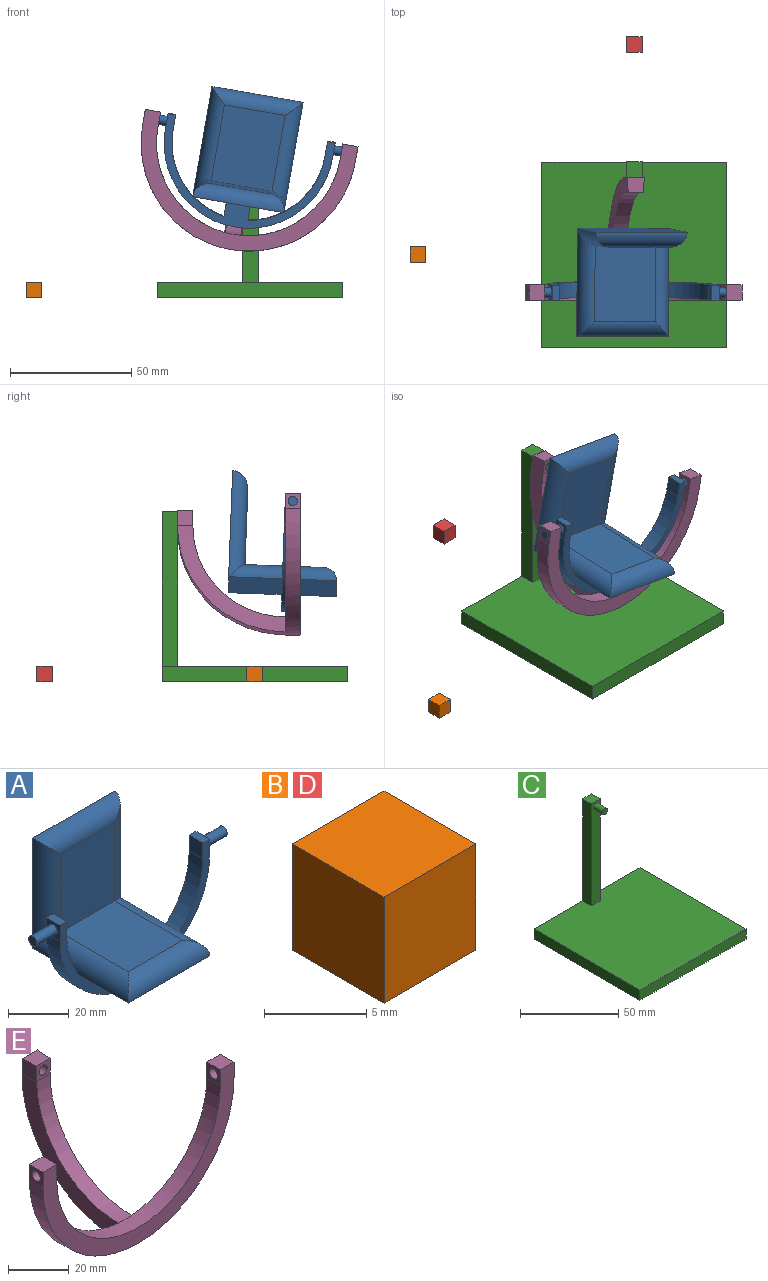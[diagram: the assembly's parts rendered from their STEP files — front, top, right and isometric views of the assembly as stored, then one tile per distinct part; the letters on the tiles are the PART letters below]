
ASSEMBLY  parts=5 mates=4
PART A: 27 faces, bbox 88.9x44.5x54.4 mm
  f0: plane 31.75x25.4mm, normal (0,0,1), area 806.5mm2, adj f20,f21,f23,f25
  f1: cylinder r=31.75mm len=31.35mm, axis (0,1,0), area 284.8mm2, adj f4,f5,f6,f16
  f2: cylinder r=31.75mm len=31.35mm, axis (0,1,0), area 284.8mm2, adj f4,f5,f10,f17
  f3: cylinder r=34.92mm len=69.85mm, axis (0,1,0), area 696.7mm2, adj f4,f5,f7,f9
  f4: plane 69.85x41.28mm, normal (0,-1,0), area 439mm2, adj f1,f2,f3,f6,f7,f8,f9,f10
  f5: plane 69.85x41.28mm, normal (0,1,0), area 439mm2, adj f1,f2,f3,f6,f7,f8,f9,f10
  f6: plane 6.35x6.35mm, normal (-1,0,0), area 40.3mm2, adj f1,f4,f5,f8
  f7: plane 6.35x6.35mm, normal (1,0,0), area 28.9mm2, adj f3,f4,f5,f8,f14
  f8: plane 6.35x3.18mm, normal (0,0,1), area 20.2mm2, adj f4,f5,f6,f7
  f9: plane 6.35x6.35mm, normal (-1,0,0), area 28.9mm2, adj f3,f4,f5,f11,f12
  f10: plane 6.35x6.35mm, normal (1,0,0), area 40.3mm2, adj f2,f4,f5,f11
  f11: plane 6.35x3.18mm, normal (0,0,1), area 20.2mm2, adj f4,f5,f9,f10
  f12: cylinder r=1.91mm len=9.53mm, axis (1,0,0), area 114mm2, adj f9,f13
  f13: plane 3.81x3.81mm, normal (-1,0,0), area 11.4mm2, adj f12
  f14: cylinder r=1.91mm len=9.53mm, axis (-1,0,0), area 114mm2, adj f7,f15
  f15: plane 3.81x3.81mm, normal (1,0,0), area 11.4mm2, adj f14
  f16: plane 6.35x6.35mm, normal (1,0,0), area 40.3mm2, adj f1,f4,f5,f19
  f17: plane 6.35x6.35mm, normal (-1,0,0), area 40.3mm2, adj f2,f4,f5,f19
  f18: plane 44.45x38.1mm, normal (0,1,0), area 1693.5mm2, adj f19,f22,f24,f26
  f19: plane 44.45x38.1mm, normal (0,0,-1), area 1630mm2, adj f4,f5,f16,f17,f18,f21,f23,f25
  f20: plane 31.75x25.4mm, normal (0,-1,0), area 806.4mm2, adj f0,f22,f24,f26
  f21: cylinder r=6.35mm len=44.45mm, axis (0,1,0), area 380mm2, adj f0,f19,f22,f23
  f22: cylinder r=6.35mm len=44.45mm, axis (0,0,-1), area 380mm2, adj f18,f20,f21,f24
  f23: cylinder r=6.35mm len=38.1mm, axis (-1,0,0), area 334mm2, adj f0,f19,f21,f25
  f24: cylinder r=6.35mm len=38.1mm, axis (-1,0,0), area 334mm2, adj f18,f20,f22,f26
  f25: cylinder r=6.35mm len=44.45mm, axis (0,-1,0), area 380mm2, adj f0,f19,f23,f26
  f26: cylinder r=6.35mm len=44.45mm, axis (0,0,1), area 380mm2, adj f18,f20,f24,f25
PART B: 6 faces, bbox 6.4x6.4x6.4 mm
  f0: plane 6.35x6.35mm, normal (0,1,0), area 40.3mm2, adj f1,f3,f4,f5
  f1: plane 6.35x6.35mm, normal (-1,0,0), area 40.3mm2, adj f0,f2,f4,f5
  f2: plane 6.35x6.35mm, normal (0,-1,0), area 40.3mm2, adj f1,f3,f4,f5
  f3: plane 6.35x6.35mm, normal (1,0,0), area 40.3mm2, adj f0,f2,f4,f5
  f4: plane 6.35x6.35mm, normal (0,0,1), area 40.3mm2, adj f0,f1,f2,f3
  f5: plane 6.35x6.35mm, normal (0,0,-1), area 40.3mm2, adj f0,f1,f2,f3
PART C: 12 faces, bbox 76.2x76.2x69.9 mm
  f0: plane 76.2x76.2mm, normal (0,0,1), area 5766.1mm2, adj f1,f2,f3,f4,f6,f7,f8
  f1: plane 76.2x69.85mm, normal (0,1,0), area 887.1mm2, adj f0,f2,f4,f5,f6,f7,f9
  f2: plane 76.2x6.35mm, normal (-1,0,0), area 483.9mm2, adj f0,f1,f3,f5
  f3: plane 76.2x6.35mm, normal (0,-1,0), area 483.9mm2, adj f0,f2,f4,f5
  f4: plane 76.2x6.35mm, normal (1,0,0), area 483.9mm2, adj f0,f1,f3,f5
  f5: plane 76.2x76.2mm, normal (0,0,-1), area 5806.4mm2, adj f1,f2,f3,f4
  f6: plane 63.5x6.35mm, normal (1,0,0), area 403.2mm2, adj f0,f1,f8,f9
  f7: plane 63.5x6.35mm, normal (-1,0,0), area 403.2mm2, adj f0,f1,f8,f9
  f8: plane 63.5x6.35mm, normal (0,-1,0), area 391.8mm2, adj f0,f6,f7,f9,f10
  f9: plane 6.35x6.35mm, normal (0,0,1), area 40.3mm2, adj f1,f6,f7,f8
  f10: cylinder r=1.91mm len=6.35mm, axis (0,1,0), area 76mm2, adj f8,f11
  f11: plane 3.81x3.81mm, normal (0,-1,0), area 11.4mm2, adj f10
PART D: same geometry as B
PART E: 24 faces, bbox 88.9x50.8x50.8 mm
  f0: plane 7.25x0.15mm, normal (0,0,1), area 0.7mm2, adj f15,f16
  f1: plane 50.65x41.34mm, normal (0,1,0), area 430.6mm2, adj f2,f3,f9,f10,f11,f14
  f2: cylinder r=44.45mm len=88.9mm, axis (0,1,0), area 886.7mm2, adj f1,f4,f5,f6,f10,f15
  f3: cylinder r=38.1mm len=76.2mm, axis (0,1,0), area 760.1mm2, adj f1,f4,f5,f7,f9,f13
  f4: plane 88.9x50.8mm, normal (0,-1,0), area 904mm2, adj f2,f3,f6,f7,f8,f9,f10,f11
  f5: plane 50.65x41.34mm, normal (0,1,0), area 430.6mm2, adj f2,f3,f6,f7,f8,f12
  f6: plane 6.35x6.35mm, normal (-1,0,0), area 28.9mm2, adj f2,f4,f5,f8,f23
  f7: plane 6.35x6.35mm, normal (1,0,0), area 28.9mm2, adj f3,f4,f5,f8,f23
  f8: plane 6.35x6.35mm, normal (0,0,1), area 40.3mm2, adj f4,f5,f6,f7
  f9: plane 6.35x6.35mm, normal (-1,0,0), area 28.9mm2, adj f1,f3,f4,f11,f22
  f10: plane 6.35x6.35mm, normal (1,0,0), area 28.9mm2, adj f1,f2,f4,f11,f22
  f11: plane 6.35x6.35mm, normal (0,0,1), area 40.3mm2, adj f1,f4,f9,f10
  f12: cone r=37.97mm half-angle=85.3deg, axis (-1,0,0), area 410.3mm2, adj f5,f13,f15,f17
  f13: sphere r=38.1mm, area 372.1mm2, adj f3,f12,f14,f18
  f14: cone r=37.97mm half-angle=85.3deg, axis (1,0,0), area 410.3mm2, adj f1,f13,f15,f19
  f15: sphere r=44.45mm, area 506.5mm2, adj f0,f2,f12,f14
  f16: plane 7.25x6.35mm, normal (0,1,0), area 34.7mm2, adj f0,f17,f19,f20,f21
  f17: plane 6.35x6.33mm, normal (-1,-0.08,0), area 40.3mm2, adj f12,f16,f18,f20
  f18: cylinder r=38.1mm len=6.35mm, axis (0,0,-1), area 28.1mm2, adj f13,f17,f19,f20,f21
  f19: plane 6.35x6.33mm, normal (1,-0.08,0), area 40.3mm2, adj f14,f16,f18,f20
  f20: plane 7.25x6.33mm, normal (0,0,1), area 42.1mm2, adj f16,f17,f18,f19
  f21: cylinder r=1.91mm len=6.25mm, axis (0,1,0), area 74.5mm2, adj f16,f18
  f22: cylinder r=1.91mm len=6.35mm, axis (-1,0,0), area 76mm2, adj f9,f10
  f23: cylinder r=1.91mm len=6.35mm, axis (-1,0,0), area 76mm2, adj f6,f7
PLACE A rot(axis=(0.21,0.98,-0.02),10.2deg) t=(-38.46,74.73,64.61)mm
PLACE B rot(axis=(1,0,0),180deg) t=(-180.41,64.96,6.35)mm
PLACE C at identity fixed
PLACE D rot(axis=(0,0,1),90deg) t=(-34.93,95.18,0)mm
PLACE E rot(axis=(0,1,0),9.9deg) t=(-38.65,-65.32,63.55)mm
MATE revolute A.f12 <-> E.f22  axis (-0.99,0,0.17) through (5.68,46.06,59.01)mm
MATE revolute C.f10 <-> E.f21  axis (0,-1,0) through (-38.1,93.53,66.68)mm
MATE slider D.f3 <-> C.f3  axis (0,1,0) through (-38.1,151.44,3.18)mm
MATE slider B.f1 <-> C.f4  axis (-1,0,0) through (-130.5,61.78,3.18)mm
